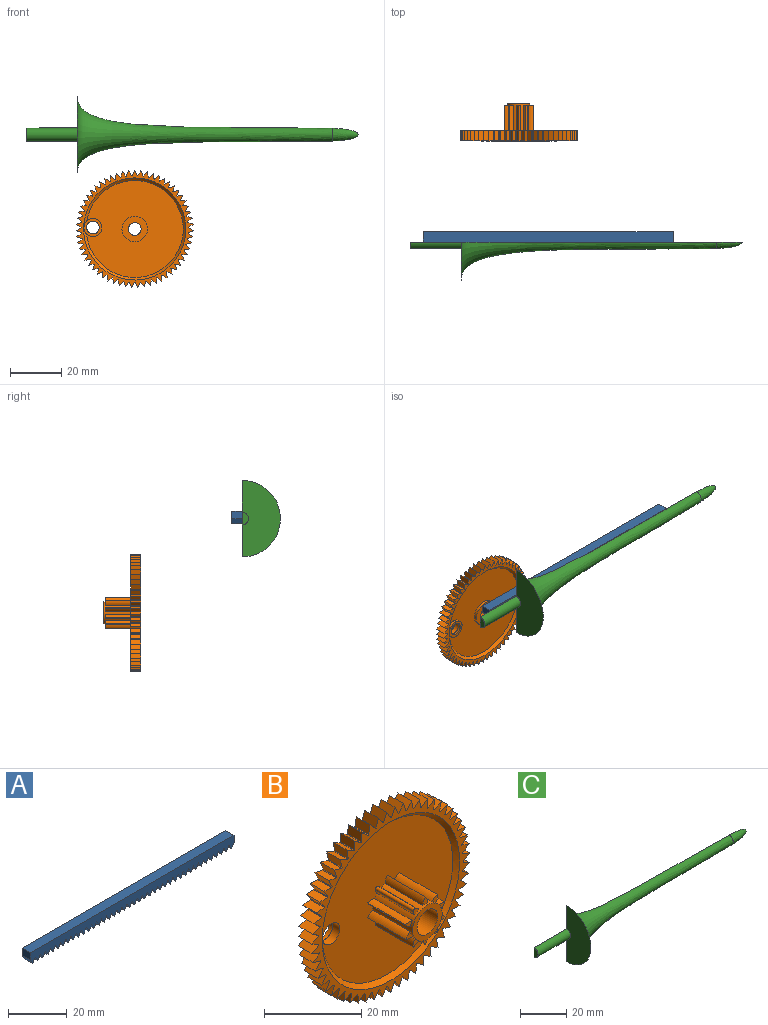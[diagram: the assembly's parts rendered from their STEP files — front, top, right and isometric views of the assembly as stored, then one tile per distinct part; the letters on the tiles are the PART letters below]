
ASSEMBLY  parts=3 mates=1
PART A: 124 faces, bbox 97.8x4x5 mm
  f0: plane 4x2mm, normal (-0.87,0,-0.5), area 9.2mm2, adj f1,f121,f122,f123
  f1: plane 4x2mm, normal (0.87,0,-0.5), area 9.2mm2, adj f0,f2,f122,f123
  f2: plane 4x0.14mm, normal (0,0,-1), area 0.6mm2, adj f1,f3,f122,f123
  f3: plane 4x2mm, normal (-0.87,0,-0.5), area 9.2mm2, adj f2,f4,f122,f123
  f4: plane 4x2mm, normal (0.87,0,-0.5), area 9.2mm2, adj f3,f5,f122,f123
  f5: plane 4x0.14mm, normal (0,0,-1), area 0.6mm2, adj f4,f6,f122,f123
  f6: plane 4x2mm, normal (-0.87,0,-0.5), area 9.2mm2, adj f5,f7,f122,f123
  f7: plane 4x2mm, normal (0.87,0,-0.5), area 9.2mm2, adj f6,f8,f122,f123
  f8: plane 4x0.14mm, normal (0,0,-1), area 0.6mm2, adj f7,f9,f122,f123
  f9: plane 4x2mm, normal (-0.87,0,-0.5), area 9.2mm2, adj f8,f10,f122,f123
  f10: plane 4x2mm, normal (0.87,0,-0.5), area 9.2mm2, adj f9,f11,f122,f123
  f11: plane 4x0.14mm, normal (0,0,-1), area 0.6mm2, adj f10,f12,f122,f123
  f12: plane 4x2mm, normal (-0.87,0,-0.5), area 9.2mm2, adj f11,f13,f122,f123
  f13: plane 4x2mm, normal (0.87,0,-0.5), area 9.2mm2, adj f12,f14,f122,f123
  f14: plane 4x0.14mm, normal (0,0,-1), area 0.6mm2, adj f13,f15,f122,f123
  f15: plane 4x2mm, normal (-0.87,0,-0.5), area 9.2mm2, adj f14,f16,f122,f123
  f16: plane 4x2mm, normal (0.87,0,-0.5), area 9.2mm2, adj f15,f17,f122,f123
  f17: plane 4x0.14mm, normal (0,0,-1), area 0.6mm2, adj f16,f18,f122,f123
  f18: plane 4x2mm, normal (-0.87,0,-0.5), area 9.2mm2, adj f17,f19,f122,f123
  f19: plane 4x2mm, normal (0.87,0,-0.5), area 9.2mm2, adj f18,f20,f122,f123
  f20: plane 4x0.14mm, normal (0,0,-1), area 0.6mm2, adj f19,f21,f122,f123
  f21: plane 4x2mm, normal (-0.87,0,-0.5), area 9.2mm2, adj f20,f22,f122,f123
  f22: plane 4x2mm, normal (0.87,0,-0.5), area 9.2mm2, adj f21,f23,f122,f123
  f23: plane 4x0.14mm, normal (0,0,-1), area 0.6mm2, adj f22,f24,f122,f123
  f24: plane 4x2mm, normal (-0.87,0,-0.5), area 9.2mm2, adj f23,f25,f122,f123
  f25: plane 4x2mm, normal (0.87,0,-0.5), area 9.2mm2, adj f24,f26,f122,f123
  f26: plane 4x0.14mm, normal (0,0,-1), area 0.6mm2, adj f25,f27,f122,f123
  f27: plane 4x2mm, normal (-0.87,0,-0.5), area 9.2mm2, adj f26,f28,f122,f123
  f28: plane 4x2mm, normal (0.87,0,-0.5), area 9.2mm2, adj f27,f29,f122,f123
  f29: plane 4x0.14mm, normal (0,0,-1), area 0.6mm2, adj f28,f30,f122,f123
  f30: plane 4x2mm, normal (-0.87,0,-0.5), area 9.2mm2, adj f29,f31,f122,f123
  f31: plane 4x2mm, normal (0.87,0,-0.5), area 9.2mm2, adj f30,f32,f122,f123
  f32: plane 4x0.14mm, normal (0,0,-1), area 0.6mm2, adj f31,f33,f122,f123
  f33: plane 4x2mm, normal (-0.87,0,-0.5), area 9.2mm2, adj f32,f34,f122,f123
  f34: plane 4x2mm, normal (0.87,0,-0.5), area 9.2mm2, adj f33,f35,f122,f123
  f35: plane 4x0.14mm, normal (0,0,-1), area 0.6mm2, adj f34,f36,f122,f123
  f36: plane 4x2mm, normal (-0.87,0,-0.5), area 9.2mm2, adj f35,f37,f122,f123
  f37: plane 4x2mm, normal (0.87,0,-0.5), area 9.2mm2, adj f36,f38,f122,f123
  f38: plane 4x0.14mm, normal (0,0,-1), area 0.6mm2, adj f37,f39,f122,f123
  f39: plane 4x2mm, normal (-0.87,0,-0.5), area 9.2mm2, adj f38,f40,f122,f123
  f40: plane 4x2mm, normal (0.87,0,-0.5), area 9.2mm2, adj f39,f41,f122,f123
  f41: plane 4x0.14mm, normal (0,0,-1), area 0.6mm2, adj f40,f42,f122,f123
  f42: plane 4x2mm, normal (-0.87,0,-0.5), area 9.2mm2, adj f41,f43,f122,f123
  f43: plane 4x2mm, normal (0.87,0,-0.5), area 9.2mm2, adj f42,f44,f122,f123
  f44: plane 4x0.14mm, normal (0,0,-1), area 0.6mm2, adj f43,f45,f122,f123
  f45: plane 4x2mm, normal (-0.87,0,-0.5), area 9.2mm2, adj f44,f46,f122,f123
  f46: plane 4x2mm, normal (0.87,0,-0.5), area 9.2mm2, adj f45,f47,f122,f123
  f47: plane 4x0.14mm, normal (0,0,-1), area 0.6mm2, adj f46,f48,f122,f123
  f48: plane 4x2mm, normal (-0.87,0,-0.5), area 9.2mm2, adj f47,f49,f122,f123
  f49: plane 4x2mm, normal (0.87,0,-0.5), area 9.2mm2, adj f48,f50,f122,f123
  f50: plane 4x0.14mm, normal (0,0,-1), area 0.6mm2, adj f49,f51,f122,f123
  f51: plane 4x2mm, normal (-0.87,0,-0.5), area 9.2mm2, adj f50,f52,f122,f123
  f52: plane 4x2mm, normal (0.87,0,-0.5), area 9.2mm2, adj f51,f53,f122,f123
  f53: plane 4x0.14mm, normal (0,0,-1), area 0.6mm2, adj f52,f54,f122,f123
  f54: plane 4x2mm, normal (-0.87,0,-0.5), area 9.2mm2, adj f53,f55,f122,f123
  f55: plane 4x2mm, normal (0.87,0,-0.5), area 9.2mm2, adj f54,f56,f122,f123
  f56: plane 4x0.14mm, normal (0,0,-1), area 0.6mm2, adj f55,f57,f122,f123
  f57: plane 4x2mm, normal (-0.87,0,-0.5), area 9.2mm2, adj f56,f58,f122,f123
  f58: plane 4x2mm, normal (0.87,0,-0.5), area 9.2mm2, adj f57,f59,f122,f123
  f59: plane 4x0.14mm, normal (0,0,-1), area 0.6mm2, adj f58,f60,f122,f123
  f60: plane 4x2mm, normal (-0.87,0,-0.5), area 9.2mm2, adj f59,f61,f122,f123
  f61: plane 4x2mm, normal (0.87,0,-0.5), area 9.2mm2, adj f60,f62,f122,f123
  f62: plane 4x0.14mm, normal (0,0,-1), area 0.6mm2, adj f61,f63,f122,f123
  f63: plane 4x2mm, normal (-0.87,0,-0.5), area 9.2mm2, adj f62,f64,f122,f123
  f64: plane 4x2mm, normal (0.87,0,-0.5), area 9.2mm2, adj f63,f65,f122,f123
  f65: plane 4x0.14mm, normal (0,0,-1), area 0.6mm2, adj f64,f66,f122,f123
  f66: plane 4x2mm, normal (-0.87,0,-0.5), area 9.2mm2, adj f65,f67,f122,f123
  f67: plane 4x2mm, normal (0.87,0,-0.5), area 9.2mm2, adj f66,f68,f122,f123
  f68: plane 4x0.14mm, normal (0,0,-1), area 0.6mm2, adj f67,f69,f122,f123
  f69: plane 4x2mm, normal (-0.87,0,-0.5), area 9.2mm2, adj f68,f70,f122,f123
  f70: plane 4x2mm, normal (0.87,0,-0.5), area 9.2mm2, adj f69,f71,f122,f123
  f71: plane 4x0.14mm, normal (0,0,-1), area 0.6mm2, adj f70,f72,f122,f123
  f72: plane 4x2mm, normal (-0.87,0,-0.5), area 9.2mm2, adj f71,f73,f122,f123
  f73: plane 4x2mm, normal (0.87,0,-0.5), area 9.2mm2, adj f72,f74,f122,f123
  f74: plane 4x0.14mm, normal (0,0,-1), area 0.6mm2, adj f73,f75,f122,f123
  f75: plane 4x2mm, normal (-0.87,0,-0.5), area 9.2mm2, adj f74,f76,f122,f123
  f76: plane 4x2mm, normal (0.87,0,-0.5), area 9.2mm2, adj f75,f77,f122,f123
  f77: plane 4x0.14mm, normal (0,0,-1), area 0.6mm2, adj f76,f78,f122,f123
  f78: plane 4x2mm, normal (-0.87,0,-0.5), area 9.2mm2, adj f77,f79,f122,f123
  f79: plane 4x2mm, normal (0.87,0,-0.5), area 9.2mm2, adj f78,f80,f122,f123
  f80: plane 4x0.14mm, normal (0,0,-1), area 0.6mm2, adj f79,f81,f122,f123
  f81: plane 4x2mm, normal (-0.87,0,-0.5), area 9.2mm2, adj f80,f82,f122,f123
  f82: plane 4x2mm, normal (0.87,0,-0.5), area 9.2mm2, adj f81,f83,f122,f123
  f83: plane 4x0.14mm, normal (0,0,-1), area 0.6mm2, adj f82,f84,f122,f123
  f84: plane 4x2mm, normal (-0.87,0,-0.5), area 9.2mm2, adj f83,f85,f122,f123
  f85: plane 4x2mm, normal (0.87,0,-0.5), area 9.2mm2, adj f84,f86,f122,f123
  f86: plane 4x0.14mm, normal (0,0,-1), area 0.6mm2, adj f85,f87,f122,f123
  f87: plane 4x2mm, normal (-0.87,0,-0.5), area 9.2mm2, adj f86,f88,f122,f123
  f88: plane 4x2mm, normal (0.87,0,-0.5), area 9.2mm2, adj f87,f89,f122,f123
  f89: plane 4x0.14mm, normal (0,0,-1), area 0.6mm2, adj f88,f90,f122,f123
  f90: plane 4x2mm, normal (-0.87,0,-0.5), area 9.2mm2, adj f89,f91,f122,f123
  f91: plane 4x2mm, normal (0.87,0,-0.5), area 9.2mm2, adj f90,f92,f122,f123
  f92: plane 4x0.14mm, normal (0,0,-1), area 0.6mm2, adj f91,f93,f122,f123
  f93: plane 4x2mm, normal (-0.87,0,-0.5), area 9.2mm2, adj f92,f94,f122,f123
  f94: plane 4x2mm, normal (0.87,0,-0.5), area 9.2mm2, adj f93,f95,f122,f123
  f95: plane 4x0.14mm, normal (0,0,-1), area 0.6mm2, adj f94,f96,f122,f123
  f96: plane 4x2mm, normal (-0.87,0,-0.5), area 9.2mm2, adj f95,f97,f122,f123
  f97: plane 4x2mm, normal (0.87,0,-0.5), area 9.2mm2, adj f96,f98,f122,f123
  f98: plane 4x0.14mm, normal (0,0,-1), area 0.6mm2, adj f97,f99,f122,f123
  f99: plane 4x2mm, normal (-0.87,0,-0.5), area 9.2mm2, adj f98,f100,f122,f123
  f100: plane 4x2mm, normal (0.87,0,-0.5), area 9.2mm2, adj f99,f101,f122,f123
  f101: plane 4x0.14mm, normal (0,0,-1), area 0.6mm2, adj f100,f102,f122,f123
  f102: plane 4x2mm, normal (-0.87,0,-0.5), area 9.2mm2, adj f101,f103,f122,f123
  f103: plane 4x2mm, normal (0.87,0,-0.5), area 9.2mm2, adj f102,f104,f122,f123
  f104: plane 4x0.14mm, normal (0,0,-1), area 0.6mm2, adj f103,f105,f122,f123
  f105: plane 4x2mm, normal (-0.87,0,-0.5), area 9.2mm2, adj f104,f106,f122,f123
  f106: plane 4x2mm, normal (0.87,0,-0.5), area 9.2mm2, adj f105,f107,f122,f123
  f107: plane 4x0.14mm, normal (0,0,-1), area 0.6mm2, adj f106,f108,f122,f123
  f108: plane 4x2mm, normal (-0.87,0,-0.5), area 9.2mm2, adj f107,f109,f122,f123
  f109: plane 4x2mm, normal (0.87,0,-0.5), area 9.2mm2, adj f108,f110,f122,f123
  f110: plane 4x0.14mm, normal (0,0,-1), area 0.6mm2, adj f109,f111,f122,f123
  f111: plane 4x2mm, normal (-0.87,0,-0.5), area 9.2mm2, adj f110,f112,f122,f123
  f112: plane 4x2mm, normal (0.87,0,-0.5), area 9.2mm2, adj f111,f113,f122,f123
  f113: plane 4x0.14mm, normal (0,0,-1), area 0.6mm2, adj f112,f114,f122,f123
  f114: plane 4x2mm, normal (-0.87,0,-0.5), area 9.2mm2, adj f113,f115,f122,f123
  f115: plane 4x2mm, normal (0.87,0,-0.5), area 9.2mm2, adj f114,f116,f122,f123
  f116: plane 4x0.14mm, normal (0,0,-1), area 0.6mm2, adj f115,f117,f122,f123
  f117: plane 4x2mm, normal (-0.87,0,-0.5), area 9.2mm2, adj f116,f118,f122,f123
  f118: plane 4x2mm, normal (0.87,0,-0.5), area 9.2mm2, adj f117,f119,f122,f123
  f119: plane 4x3mm, normal (1,0,0), area 12mm2, adj f118,f120,f122,f123
  f120: plane 97.76x4mm, normal (0,0,1), area 391mm2, adj f119,f121,f122,f123
  f121: plane 4x3mm, normal (-1,0,0), area 12mm2, adj f0,f120,f122,f123
  f122: plane 97.76x5mm, normal (0,-1,0), area 385.6mm2, adj f0,f1,f2,f3,f4,f5,f6,f7
  f123: plane 97.76x5mm, normal (0,1,0), area 385.6mm2, adj f0,f1,f2,f3,f4,f5,f6,f7
PART B: 228 faces, bbox 46x14.6x46 mm
  f0: plane 4.63x3.92mm, normal (0,1,0), area 0.1mm2, adj f223,f225
  f1: plane 1.63x1.59mm, normal (0,-1,0), area 1.5mm2, adj f13,f26,f27,f222
  f2: plane 1.89x1.46mm, normal (0,-1,0), area 1.6mm2, adj f13,f24,f25
  f3: plane 1.89x1.46mm, normal (0,-1,0), area 1.6mm2, adj f13,f22,f23
  f4: plane 1.83x1.62mm, normal (0,-1,0), area 1.6mm2, adj f13,f20,f21
  f5: plane 1.76x1.4mm, normal (0,-1,0), area 1.6mm2, adj f13,f18,f19
  f6: plane 1.63x1.59mm, normal (0,-1,0), area 1.5mm2, adj f13,f16,f17,f221
  f7: plane 1.89x1.46mm, normal (0,-1,0), area 1.6mm2, adj f13,f14,f15
  f8: plane 1.89x1.46mm, normal (0,-1,0), area 1.6mm2, adj f10,f11,f13
  f9: plane 1.83x1.62mm, normal (0,-1,0), area 1.6mm2, adj f13,f30,f31
  f10: cylinder r=2.56mm len=11mm, axis (0,1,0), area 21.3mm2, adj f8,f11,f13,f214
  f11: cylinder r=2.56mm len=11mm, axis (0,1,0), area 21.3mm2, adj f8,f10,f13,f214
  f12: plane 1.76x1.4mm, normal (0,-1,0), area 1.6mm2, adj f13,f28,f29
  f13: cylinder r=4.3mm len=11.6mm, axis (0,1,0), area 158.9mm2, adj f1,f2,f3,f4,f5,f6,f7,f8
  f14: cylinder r=2.56mm len=11mm, axis (0,1,0), area 21.3mm2, adj f7,f13,f15,f214
  f15: cylinder r=2.56mm len=11mm, axis (0,1,0), area 21.3mm2, adj f7,f13,f14,f214
  f16: cylinder r=2.56mm len=11mm, axis (0,1,0), area 12.5mm2, adj f6,f13,f214,f221
  f17: cylinder r=2.56mm len=11mm, axis (0,1,0), area 12.5mm2, adj f6,f13,f214,f221
  f18: cylinder r=2.56mm len=11mm, axis (0,1,0), area 21.3mm2, adj f5,f13,f19,f214
  f19: cylinder r=2.56mm len=11mm, axis (0,1,0), area 21.3mm2, adj f5,f13,f18,f214
  f20: cylinder r=2.56mm len=11mm, axis (0,1,0), area 21.3mm2, adj f4,f13,f21,f214
  f21: cylinder r=2.56mm len=11mm, axis (0,1,0), area 21.3mm2, adj f4,f13,f20,f214
  f22: cylinder r=2.56mm len=11mm, axis (0,1,0), area 21.3mm2, adj f3,f13,f23,f214
  f23: cylinder r=2.56mm len=11mm, axis (0,1,0), area 21.3mm2, adj f3,f13,f22,f214
  f24: cylinder r=2.56mm len=11mm, axis (0,1,0), area 21.3mm2, adj f2,f13,f25,f214
  f25: cylinder r=2.56mm len=11mm, axis (0,1,0), area 21.3mm2, adj f2,f13,f24,f214
  f26: cylinder r=2.56mm len=11mm, axis (0,1,0), area 12.5mm2, adj f1,f13,f214,f222
  f27: cylinder r=2.56mm len=11mm, axis (0,1,0), area 12.5mm2, adj f1,f13,f214,f222
  f28: cylinder r=2.56mm len=11mm, axis (0,1,0), area 21.3mm2, adj f12,f13,f29,f214
  f29: cylinder r=2.56mm len=11mm, axis (0,1,0), area 21.3mm2, adj f12,f13,f28,f214
  f30: cylinder r=2.56mm len=11mm, axis (0,1,0), area 21.3mm2, adj f9,f13,f31,f214
  f31: cylinder r=2.56mm len=11mm, axis (0,1,0), area 21.3mm2, adj f9,f13,f30,f214
  f32: cylinder r=3mm len=13.6mm, axis (0,1,0), area 256.4mm2, adj f33,f215
  f33: plane 8.6x8.6mm, normal (0,-1,0), area 29.8mm2, adj f13,f32
  f34: cylinder r=21mm len=4mm, axis (0,1,0), area 0.9mm2, adj f93,f94,f97,f212
  f35: cylinder r=21mm len=4mm, axis (0,1,0), area 0.9mm2, adj f93,f94,f210,f213
  f36: cylinder r=21mm len=4mm, axis (0,1,0), area 0.9mm2, adj f93,f94,f208,f211
  f37: cylinder r=21mm len=4mm, axis (0,1,0), area 0.9mm2, adj f93,f94,f206,f209
  f38: cylinder r=21mm len=4mm, axis (0,1,0), area 0.9mm2, adj f93,f94,f204,f207
  f39: cylinder r=21mm len=4mm, axis (0,1,0), area 0.9mm2, adj f93,f94,f202,f205
  f40: cylinder r=21mm len=4mm, axis (0,1,0), area 0.9mm2, adj f93,f94,f200,f203
  f41: cylinder r=21mm len=4mm, axis (0,1,0), area 0.9mm2, adj f93,f94,f198,f201
  f42: cylinder r=21mm len=4mm, axis (0,1,0), area 0.9mm2, adj f93,f94,f196,f199
  f43: cylinder r=21mm len=4mm, axis (0,1,0), area 0.9mm2, adj f93,f94,f194,f197
  f44: cylinder r=21mm len=4mm, axis (0,1,0), area 0.9mm2, adj f93,f94,f192,f195
  f45: cylinder r=21mm len=4mm, axis (0,1,0), area 0.9mm2, adj f93,f94,f190,f193
  f46: cylinder r=21mm len=4mm, axis (0,1,0), area 0.9mm2, adj f93,f94,f188,f191
  f47: cylinder r=21mm len=4mm, axis (0,1,0), area 0.9mm2, adj f93,f94,f186,f189
  f48: cylinder r=21mm len=4mm, axis (0,1,0), area 0.9mm2, adj f93,f94,f184,f187
  f49: cylinder r=21mm len=4mm, axis (0,1,0), area 0.9mm2, adj f93,f94,f182,f185
  f50: cylinder r=21mm len=4mm, axis (0,1,0), area 0.9mm2, adj f93,f94,f180,f183
  f51: cylinder r=21mm len=4mm, axis (0,1,0), area 0.9mm2, adj f93,f94,f178,f181
  f52: cylinder r=21mm len=4mm, axis (0,1,0), area 0.9mm2, adj f93,f94,f176,f179
  f53: cylinder r=21mm len=4mm, axis (0,1,0), area 0.9mm2, adj f93,f94,f174,f177
  f54: cylinder r=21mm len=4mm, axis (0,1,0), area 0.9mm2, adj f93,f94,f172,f175
  f55: cylinder r=21mm len=4mm, axis (0,1,0), area 0.9mm2, adj f93,f94,f170,f173
  f56: cylinder r=21mm len=4mm, axis (0,1,0), area 0.9mm2, adj f93,f94,f168,f171
  f57: cylinder r=21mm len=4mm, axis (0,1,0), area 0.9mm2, adj f93,f94,f166,f169
  f58: cylinder r=21mm len=4mm, axis (0,1,0), area 0.9mm2, adj f93,f94,f164,f167
  f59: cylinder r=21mm len=4mm, axis (0,1,0), area 0.9mm2, adj f93,f94,f162,f165
  f60: cylinder r=21mm len=4mm, axis (0,1,0), area 0.9mm2, adj f93,f94,f160,f163
  f61: cylinder r=21mm len=4mm, axis (0,1,0), area 0.9mm2, adj f93,f94,f158,f161
  f62: cylinder r=21mm len=4mm, axis (0,1,0), area 0.9mm2, adj f93,f94,f156,f159
  f63: cylinder r=21mm len=4mm, axis (0,1,0), area 0.9mm2, adj f93,f94,f154,f157
  f64: cylinder r=21mm len=4mm, axis (0,1,0), area 0.9mm2, adj f93,f94,f152,f155
  f65: cylinder r=21mm len=4mm, axis (0,1,0), area 0.9mm2, adj f93,f94,f150,f153
  f66: cylinder r=21mm len=4mm, axis (0,1,0), area 0.9mm2, adj f93,f94,f148,f151
  f67: cylinder r=21mm len=4mm, axis (0,1,0), area 0.9mm2, adj f93,f94,f146,f149
  f68: cylinder r=21mm len=4mm, axis (0,1,0), area 0.9mm2, adj f93,f94,f144,f147
  f69: cylinder r=21mm len=4mm, axis (0,1,0), area 0.9mm2, adj f93,f94,f142,f145
  f70: cylinder r=21mm len=4mm, axis (0,1,0), area 0.9mm2, adj f93,f94,f140,f143
  f71: cylinder r=21mm len=4mm, axis (0,1,0), area 0.9mm2, adj f93,f94,f138,f141
  f72: cylinder r=21mm len=4mm, axis (0,1,0), area 0.9mm2, adj f93,f94,f136,f139
  f73: cylinder r=21mm len=4mm, axis (0,1,0), area 0.9mm2, adj f93,f94,f134,f137
  f74: cylinder r=21mm len=4mm, axis (0,1,0), area 0.9mm2, adj f93,f94,f132,f135
  f75: cylinder r=21mm len=4mm, axis (0,1,0), area 0.9mm2, adj f93,f94,f130,f133
  f76: cylinder r=21mm len=4mm, axis (0,1,0), area 0.9mm2, adj f93,f94,f128,f131
  f77: cylinder r=21mm len=4mm, axis (0,1,0), area 0.9mm2, adj f93,f94,f126,f129
  f78: cylinder r=21mm len=4mm, axis (0,1,0), area 0.9mm2, adj f93,f94,f124,f127
  f79: cylinder r=21mm len=4mm, axis (0,1,0), area 0.9mm2, adj f93,f94,f122,f125
  f80: cylinder r=21mm len=4mm, axis (0,1,0), area 0.9mm2, adj f93,f94,f120,f123
  f81: cylinder r=21mm len=4mm, axis (0,1,0), area 0.9mm2, adj f93,f94,f118,f121
  f82: cylinder r=21mm len=4mm, axis (0,1,0), area 0.9mm2, adj f93,f94,f116,f119
  f83: cylinder r=21mm len=4mm, axis (0,1,0), area 0.9mm2, adj f93,f94,f114,f117
  f84: cylinder r=21mm len=4mm, axis (0,1,0), area 0.9mm2, adj f93,f94,f112,f115
  f85: cylinder r=21mm len=4mm, axis (0,1,0), area 0.9mm2, adj f93,f94,f110,f113
  f86: cylinder r=21mm len=4mm, axis (0,1,0), area 0.9mm2, adj f93,f94,f108,f111
  f87: cylinder r=21mm len=4mm, axis (0,1,0), area 0.9mm2, adj f93,f94,f106,f109
  f88: cylinder r=21mm len=4mm, axis (0,1,0), area 0.9mm2, adj f93,f94,f104,f107
  f89: cylinder r=21mm len=4mm, axis (0,1,0), area 0.9mm2, adj f93,f94,f102,f105
  f90: cylinder r=21mm len=4mm, axis (0,1,0), area 0.9mm2, adj f93,f94,f100,f103
  f91: cylinder r=21mm len=4mm, axis (0,1,0), area 0.9mm2, adj f93,f94,f98,f101
  f92: cylinder r=21mm len=4mm, axis (0,1,0), area 0.9mm2, adj f93,f94,f96,f99
  f93: plane 45.98x45.97mm, normal (0,-1,0), area 246.3mm2, adj f34,f35,f36,f37,f38,f39,f40,f41
  f94: plane 45.98x45.97mm, normal (0,1,0), area 246.3mm2, adj f34,f35,f36,f37,f38,f39,f40,f41
  f95: plane 38x37.91mm, normal (0,1,0), area 1020.2mm2, adj f217,f220,f226
  f96: plane 4x2.02mm, normal (-0.9,0,-0.44), area 9mm2, adj f92,f93,f94,f97
  f97: plane 4x2.02mm, normal (0.9,0,-0.44), area 9mm2, adj f34,f93,f94,f96
  f98: plane 4x2.12mm, normal (-0.94,0,-0.35), area 9mm2, adj f91,f93,f94,f99
  f99: plane 4x1.91mm, normal (0.84,0,-0.54), area 9mm2, adj f92,f93,f94,f98
  f100: plane 4x2.19mm, normal (-0.97,0,-0.24), area 9mm2, adj f90,f93,f94,f101
  f101: plane 4x1.77mm, normal (0.78,0,-0.62), area 9mm2, adj f91,f93,f94,f100
  f102: plane 4x2.24mm, normal (-0.99,0,-0.14), area 9mm2, adj f89,f93,f94,f103
  f103: plane 4x1.61mm, normal (0.71,0,-0.7), area 9mm2, adj f90,f93,f94,f102
  f104: plane 4x2.26mm, normal (-1,0,-0.03), area 9mm2, adj f88,f93,f94,f105
  f105: plane 4x1.75mm, normal (0.63,0,-0.77), area 9mm2, adj f89,f93,f94,f104
  f106: plane 4x2.25mm, normal (-1,0,0.07), area 9mm2, adj f87,f93,f94,f107
  f107: plane 4x1.89mm, normal (0.55,0,-0.84), area 9mm2, adj f88,f93,f94,f106
  f108: plane 4x2.22mm, normal (-0.98,0,0.18), area 9mm2, adj f86,f93,f94,f109
  f109: plane 4x2.01mm, normal (0.46,0,-0.89), area 9mm2, adj f87,f93,f94,f108
  f110: plane 4x2.17mm, normal (-0.96,0,0.28), area 9mm2, adj f85,f93,f94,f111
  f111: plane 4x2.11mm, normal (0.36,0,-0.93), area 9mm2, adj f86,f93,f94,f110
  f112: plane 4x2.09mm, normal (-0.92,0,0.38), area 9mm2, adj f84,f93,f94,f113
  f113: plane 4x2.18mm, normal (0.26,0,-0.97), area 9mm2, adj f85,f93,f94,f112
  f114: plane 4x1.98mm, normal (-0.88,0,0.48), area 9mm2, adj f83,f93,f94,f115
  f115: plane 4x2.23mm, normal (0.15,0,-0.99), area 9mm2, adj f84,f93,f94,f114
  f116: plane 4x1.86mm, normal (-0.82,0,0.57), area 9mm2, adj f82,f93,f94,f117
  f117: plane 4x2.26mm, normal (0.05,0,-1), area 9mm2, adj f83,f93,f94,f116
  f118: plane 4x1.71mm, normal (-0.76,0,0.65), area 9mm2, adj f81,f93,f94,f119
  f119: plane 4x2.25mm, normal (-0.06,0,-1), area 9mm2, adj f82,f93,f94,f118
  f120: plane 4x1.65mm, normal (-0.68,0,0.73), area 9mm2, adj f80,f93,f94,f121
  f121: plane 4x2.23mm, normal (-0.17,0,-0.99), area 9mm2, adj f81,f93,f94,f120
  f122: plane 4x1.8mm, normal (-0.6,0,0.8), area 9mm2, adj f79,f93,f94,f123
  f123: plane 4x2.17mm, normal (-0.27,0,-0.96), area 9mm2, adj f80,f93,f94,f122
  f124: plane 4x1.94mm, normal (-0.51,0,0.86), area 9mm2, adj f78,f93,f94,f125
  f125: plane 4x2.1mm, normal (-0.37,0,-0.93), area 9mm2, adj f79,f93,f94,f124
  f126: plane 4x2.05mm, normal (-0.42,0,0.91), area 9mm2, adj f77,f93,f94,f127
  f127: plane 4x2mm, normal (-0.47,0,-0.88), area 9mm2, adj f78,f93,f94,f126
  f128: plane 4x2.14mm, normal (-0.32,0,0.95), area 9mm2, adj f76,f93,f94,f129
  f129: plane 4x1.87mm, normal (-0.56,0,-0.83), area 9mm2, adj f77,f93,f94,f128
  f130: plane 4x2.2mm, normal (-0.22,0,0.98), area 9mm2, adj f75,f93,f94,f131
  f131: plane 4x1.73mm, normal (-0.64,0,-0.77), area 9mm2, adj f76,f93,f94,f130
  f132: plane 4x2.24mm, normal (-0.11,0,0.99), area 9mm2, adj f74,f93,f94,f133
  f133: plane 4x1.63mm, normal (-0.72,0,-0.69), area 9mm2, adj f75,f93,f94,f132
  f134: plane 4x2.26mm, normal (-0.01,0,1), area 9mm2, adj f73,f93,f94,f135
  f135: plane 4x1.78mm, normal (-0.79,0,-0.61), area 9mm2, adj f74,f93,f94,f134
  f136: plane 4x2.25mm, normal (0.1,0,0.99), area 9mm2, adj f72,f93,f94,f137
  f137: plane 4x1.92mm, normal (-0.85,0,-0.53), area 9mm2, adj f73,f93,f94,f136
  f138: plane 4x2.21mm, normal (0.21,0,0.98), area 9mm2, adj f71,f93,f94,f139
  f139: plane 4x2.04mm, normal (-0.9,0,-0.43), area 9mm2, adj f72,f93,f94,f138
  f140: plane 4x2.15mm, normal (0.31,0,0.95), area 9mm2, adj f70,f93,f94,f141
  f141: plane 4x2.13mm, normal (-0.94,0,-0.33), area 9mm2, adj f71,f93,f94,f140
  f142: plane 4x2.06mm, normal (0.41,0,0.91), area 9mm2, adj f69,f93,f94,f143
  f143: plane 4x2.2mm, normal (-0.97,0,-0.23), area 9mm2, adj f70,f93,f94,f142
  f144: plane 4x1.95mm, normal (0.5,0,0.86), area 9mm2, adj f68,f93,f94,f145
  f145: plane 4x2.24mm, normal (-0.99,0,-0.13), area 9mm2, adj f69,f93,f94,f144
  f146: plane 4x1.82mm, normal (0.59,0,0.81), area 9mm2, adj f67,f93,f94,f147
  f147: plane 4x2.26mm, normal (-1,0,-0.02), area 9mm2, adj f68,f93,f94,f146
  f148: plane 4x1.67mm, normal (0.67,0,0.74), area 9mm2, adj f66,f93,f94,f149
  f149: plane 4x2.25mm, normal (-1,0,0.09), area 9mm2, adj f67,f93,f94,f148
  f150: plane 4x1.69mm, normal (0.75,0,0.66), area 9mm2, adj f65,f93,f94,f151
  f151: plane 4x2.22mm, normal (-0.98,0,0.19), area 9mm2, adj f66,f93,f94,f150
  f152: plane 4x1.84mm, normal (0.81,0,0.58), area 9mm2, adj f64,f93,f94,f153
  f153: plane 4x2.16mm, normal (-0.96,0,0.29), area 9mm2, adj f65,f93,f94,f152
  f154: plane 4x1.97mm, normal (0.87,0,0.49), area 9mm2, adj f63,f93,f94,f155
  f155: plane 4x2.07mm, normal (-0.92,0,0.39), area 9mm2, adj f64,f93,f94,f154
  f156: plane 4x2.07mm, normal (0.92,0,0.39), area 9mm2, adj f62,f93,f94,f157
  f157: plane 4x1.97mm, normal (-0.87,0,0.49), area 9mm2, adj f63,f93,f94,f156
  f158: plane 4x2.16mm, normal (0.96,0,0.29), area 9mm2, adj f61,f93,f94,f159
  f159: plane 4x1.84mm, normal (-0.81,0,0.58), area 9mm2, adj f62,f93,f94,f158
  f160: plane 4x2.22mm, normal (0.98,0,0.19), area 9mm2, adj f60,f93,f94,f161
  f161: plane 4x1.69mm, normal (-0.75,0,0.66), area 9mm2, adj f61,f93,f94,f160
  f162: plane 4x2.25mm, normal (1,0,0.09), area 9mm2, adj f59,f93,f94,f163
  f163: plane 4x1.67mm, normal (-0.67,0,0.74), area 9mm2, adj f60,f93,f94,f162
  f164: plane 4x2.26mm, normal (1,0,-0.02), area 9mm2, adj f58,f93,f94,f165
  f165: plane 4x1.82mm, normal (-0.59,0,0.81), area 9mm2, adj f59,f93,f94,f164
  f166: plane 4x2.24mm, normal (0.99,0,-0.13), area 9mm2, adj f57,f93,f94,f167
  f167: plane 4x1.95mm, normal (-0.5,0,0.86), area 9mm2, adj f58,f93,f94,f166
  f168: plane 4x2.2mm, normal (0.97,0,-0.23), area 9mm2, adj f56,f93,f94,f169
  f169: plane 4x2.06mm, normal (-0.41,0,0.91), area 9mm2, adj f57,f93,f94,f168
  f170: plane 4x2.13mm, normal (0.94,0,-0.33), area 9mm2, adj f55,f93,f94,f171
  f171: plane 4x2.15mm, normal (-0.31,0,0.95), area 9mm2, adj f56,f93,f94,f170
  f172: plane 4x2.04mm, normal (0.9,0,-0.43), area 9mm2, adj f54,f93,f94,f173
  f173: plane 4x2.21mm, normal (-0.21,0,0.98), area 9mm2, adj f55,f93,f94,f172
  f174: plane 4x1.92mm, normal (0.85,0,-0.53), area 9mm2, adj f53,f93,f94,f175
  f175: plane 4x2.25mm, normal (-0.1,0,0.99), area 9mm2, adj f54,f93,f94,f174
  f176: plane 4x1.78mm, normal (0.79,0,-0.61), area 9mm2, adj f52,f93,f94,f177
  f177: plane 4x2.26mm, normal (0.01,0,1), area 9mm2, adj f53,f93,f94,f176
  f178: plane 4x1.63mm, normal (0.72,0,-0.69), area 9mm2, adj f51,f93,f94,f179
  f179: plane 4x2.24mm, normal (0.11,0,0.99), area 9mm2, adj f52,f93,f94,f178
  f180: plane 4x1.73mm, normal (0.64,0,-0.77), area 9mm2, adj f50,f93,f94,f181
  f181: plane 4x2.2mm, normal (0.22,0,0.98), area 9mm2, adj f51,f93,f94,f180
  f182: plane 4x1.87mm, normal (0.56,0,-0.83), area 9mm2, adj f49,f93,f94,f183
  f183: plane 4x2.14mm, normal (0.32,0,0.95), area 9mm2, adj f50,f93,f94,f182
  f184: plane 4x2mm, normal (0.47,0,-0.88), area 9mm2, adj f48,f93,f94,f185
  f185: plane 4x2.05mm, normal (0.42,0,0.91), area 9mm2, adj f49,f93,f94,f184
  f186: plane 4x2.1mm, normal (0.37,0,-0.93), area 9mm2, adj f47,f93,f94,f187
  f187: plane 4x1.94mm, normal (0.51,0,0.86), area 9mm2, adj f48,f93,f94,f186
  f188: plane 4x2.17mm, normal (0.27,0,-0.96), area 9mm2, adj f46,f93,f94,f189
  f189: plane 4x1.8mm, normal (0.6,0,0.8), area 9mm2, adj f47,f93,f94,f188
  f190: plane 4x2.23mm, normal (0.17,0,-0.99), area 9mm2, adj f45,f93,f94,f191
  f191: plane 4x1.65mm, normal (0.68,0,0.73), area 9mm2, adj f46,f93,f94,f190
  f192: plane 4x2.25mm, normal (0.06,0,-1), area 9mm2, adj f44,f93,f94,f193
  f193: plane 4x1.71mm, normal (0.76,0,0.65), area 9mm2, adj f45,f93,f94,f192
  f194: plane 4x2.26mm, normal (-0.05,0,-1), area 9mm2, adj f43,f93,f94,f195
  f195: plane 4x1.86mm, normal (0.82,0,0.57), area 9mm2, adj f44,f93,f94,f194
  f196: plane 4x2.23mm, normal (-0.15,0,-0.99), area 9mm2, adj f42,f93,f94,f197
  f197: plane 4x1.98mm, normal (0.88,0,0.48), area 9mm2, adj f43,f93,f94,f196
  f198: plane 4x2.18mm, normal (-0.26,0,-0.97), area 9mm2, adj f41,f93,f94,f199
  f199: plane 4x2.09mm, normal (0.92,0,0.38), area 9mm2, adj f42,f93,f94,f198
  f200: plane 4x2.11mm, normal (-0.36,0,-0.93), area 9mm2, adj f40,f93,f94,f201
  f201: plane 4x2.17mm, normal (0.96,0,0.28), area 9mm2, adj f41,f93,f94,f200
  f202: plane 4x2.01mm, normal (-0.46,0,-0.89), area 9mm2, adj f39,f93,f94,f203
  f203: plane 4x2.22mm, normal (0.98,0,0.18), area 9mm2, adj f40,f93,f94,f202
  f204: plane 4x1.89mm, normal (-0.55,0,-0.84), area 9mm2, adj f38,f93,f94,f205
  f205: plane 4x2.25mm, normal (1,0,0.07), area 9mm2, adj f39,f93,f94,f204
  f206: plane 4x1.75mm, normal (-0.63,0,-0.77), area 9mm2, adj f37,f93,f94,f207
  f207: plane 4x2.26mm, normal (1,0,-0.03), area 9mm2, adj f38,f93,f94,f206
  f208: plane 4x1.61mm, normal (-0.71,0,-0.7), area 9mm2, adj f36,f93,f94,f209
  f209: plane 4x2.24mm, normal (0.99,0,-0.14), area 9mm2, adj f37,f93,f94,f208
  f210: plane 4x1.77mm, normal (-0.78,0,-0.62), area 9mm2, adj f35,f93,f94,f211
  f211: plane 4x2.19mm, normal (0.97,0,-0.24), area 9mm2, adj f36,f93,f94,f210
  f212: plane 4x1.91mm, normal (-0.84,0,-0.54), area 9mm2, adj f34,f93,f94,f213
  f213: plane 4x2.12mm, normal (0.94,0,-0.35), area 9mm2, adj f35,f93,f94,f212
  f214: plane 38x38mm, normal (0,-1,0), area 1040.3mm2, adj f10,f11,f13,f14,f15,f16,f17,f18
  f215: plane 6x6mm, normal (0,-1,0), area 8.6mm2, adj f32,f218
  f216: plane 10x10mm, normal (0,1,0), area 58.9mm2, adj f217,f218
  f217: cylinder r=5mm len=10mm, axis (0,-1,0), area 31.4mm2, adj f95,f216
  f218: cylinder r=2.5mm len=5mm, axis (0,-1,0), area 15.7mm2, adj f215,f216
  f219: cone r=19mm half-angle=45deg, axis (0,-1,0), area 173.3mm2, adj f93,f214
  f220: cone r=20mm half-angle=45deg, axis (0,1,0), area 168.8mm2, adj f94,f95,f226
  f221: cylinder r=0.5mm len=11mm, axis (0,1,0), area 12.4mm2, adj f6,f16,f17,f214
  f222: cylinder r=0.5mm len=11mm, axis (0,1,0), area 12.4mm2, adj f1,f26,f27,f214
  f223: cylinder r=2.5mm len=5mm, axis (0,-1,0), area 31.4mm2, adj f0,f214,f224
  f224: plane 4.57x3.83mm, normal (0,-1,0), area 0.1mm2, adj f223,f225
  f225: cylinder r=2.5mm len=5mm, axis (0,1,0), area 15.7mm2, adj f0,f224,f227
  f226: cylinder r=3.5mm len=7.01mm, axis (0,1,0), area 18.7mm2, adj f95,f220,f227
  f227: plane 7.01x7.01mm, normal (0,1,0), area 18.9mm2, adj f225,f226
PART C: 6 faces, bbox 130x15x30 mm
  f0: cylinder r=2.5mm len=20mm, axis (-1,0,0), area 157.1mm2, adj f1,f2,f5
  f1: plane 5x2.5mm, normal (-1,0,0), area 9.8mm2, adj f0,f5
  f2: plane 30x15mm, normal (-1,0,0), area 343.6mm2, adj f0,f4,f5
  f3: revolved ~10x5mm, area 62.4mm2, adj f4,f5
  f4: revolved ~100x30mm, area 1336.2mm2, adj f2,f3,f5
  f5: plane 130.01x30mm, normal (0,1,0), area 882.2mm2, adj f0,f1,f2,f3,f4
PLACE A t=(-19.84,-4.2,10.74)mm
PLACE B rot(axis=(-1,0,0),180deg) t=(-31.4,31.47,-27.68)mm
PLACE C t=(-3.98,-8.2,9.24)mm
MATE fastened C.f5 <-> A.f122  axis (0,1,0) through (-17.32,-8.2,9.24)mm
